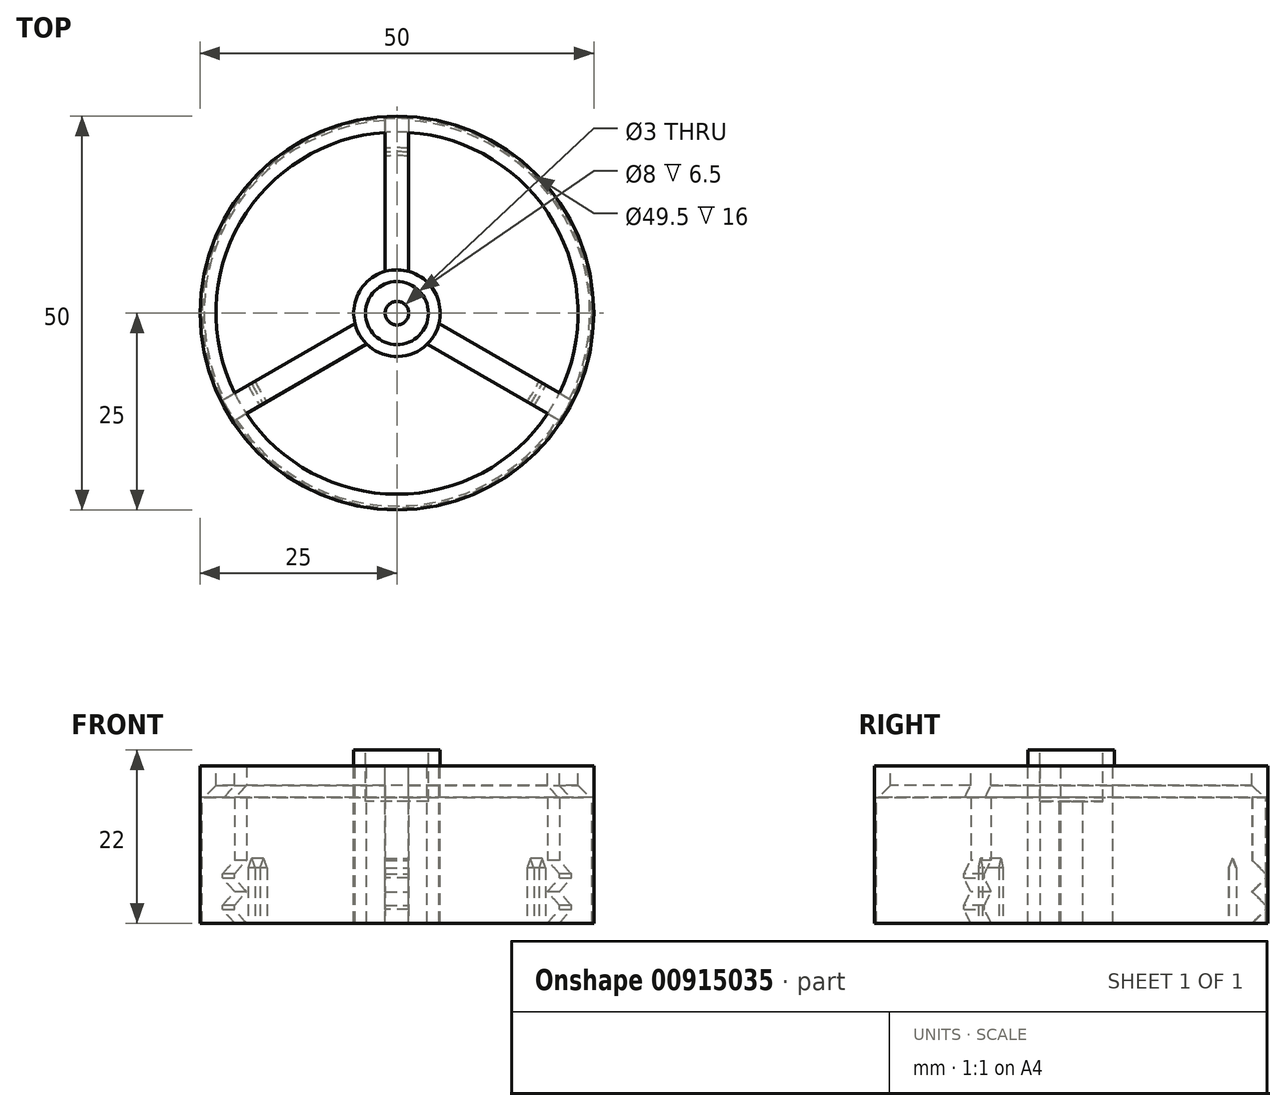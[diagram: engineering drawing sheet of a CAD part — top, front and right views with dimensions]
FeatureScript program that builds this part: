
annotation { "Feature Type Name" : "Feature", "Feature Type Description" : "" }
export const myFeature = defineFeature(function(context is Context, id is Id, definition is map)
    precondition{}
    {
        {
            var Q0;
            Q0=qCreatedBy(makeId("Front.planeOp"),FACE);
            var sketch = newSketch(context, id + "F0", { "sketchPlane" : qUnion([Q0])});
            skLineSegment(sketch, "E0", {"start": v(23, 0) * mm, "end": v(23, 12) * mm});
            skLineSegment(sketch, "E1", {"start": v(23, 12) * mm, "end": v(25, 14) * mm});
            skLineSegment(sketch, "E2", {"start": v(25, 14) * mm, "end": v(23, 16) * mm});
            skLineSegment(sketch, "E3", {"start": v(23, 16) * mm, "end": v(25, 18) * mm});
            skLineSegment(sketch, "E4", {"start": v(25, 18) * mm, "end": v(23, 20) * mm});
            skLineSegment(sketch, "E5", {"start": v(23, 20) * mm, "end": v(0, 20) * mm});
            skLineSegment(sketch, "E6", {"start": v(0, 20) * mm, "end": v(0, 0) * mm});
            skLineSegment(sketch, "E7", {"start": v(0, 0) * mm, "end": v(23, 0) * mm});
            skLineSegment(sketch, "E8", {"start": v(21, 20) * mm, "end": v(21, 13) * mm});
            skLineSegment(sketch, "E9", {"start": v(20, 13) * mm, "end": v(20, 20) * mm});
            skLineSegment(sketch, "E10", {"start": v(20, 13) * mm, "end": v(20.5, 11.8) * mm});
            skLineSegment(sketch, "E11", {"start": v(20.5, 11.8) * mm, "end": v(21, 13) * mm});
            skSolve(sketch);
        }
        {
            var Q0;
            Q0=makeQuery(id+"F0.imprint","IMPRINT",FACE,{"disambiguationData":[TD([[makeQuery(id+"F0.imprint","IMPRINT",EDGE,{"derivedFrom":sQuery(id+"F0.wireOp",EDGE,"E0")}),1.0]])]});
            var Q1;
            Q1=sQuery(id+"F0.wireOp",EDGE,"E6");
            revolve(context, id + "F1", {"surfaceOperationType" : NewSurfaceOperationType.NEW, "entities" : qUnion([Q0]), "axis" : qUnion([Q1]), "revolveType" : RevolveType.FULL});
        }
        {
            var Q0;
            Q0=qCreatedBy(makeId("Top.planeOp"),FACE);
            var sketch = newSketch(context, id + "F2", { "sketchPlane" : qUnion([Q0])});
            skCircle(sketch, "E12", {"center": v(0, 0) * mm, "radius": 25 * mm});
            skCircle(sketch, "E13", {"center": v(0, 0) * mm, "radius": 4 * mm});
            skCircle(sketch, "E14", {"center": v(0, 0) * mm, "radius": 5.5 * mm});
            skLineSegment(sketch, "E15", {"start": v(-31.51, 0) * mm, "end": v(37.3, 0) * mm, "construction": true});
            skLineSegment(sketch, "E16", {"start": v(0, 27.34) * mm, "end": v(0, -29.3) * mm, "construction": true});
            skLineSegment(sketch, "E17", {"start": v(-1.5, -5.3) * mm, "end": v(-1.5, -24.95) * mm});
            skLineSegment(sketch, "E18", {"start": v(1.5, -5.3) * mm, "end": v(1.5, -24.95) * mm});
            skLineSegment(sketch, "E19", {"start": v(-5.33, 1.35) * mm, "end": v(-22.36, 11.18) * mm});
            skLineSegment(sketch, "E20", {"start": v(-3.83, 3.94) * mm, "end": v(-20.86, 13.78) * mm});
            skLineSegment(sketch, "E21", {"start": v(3.83, 3.94) * mm, "end": v(20.86, 13.78) * mm});
            skLineSegment(sketch, "E22", {"start": v(5.33, 1.35) * mm, "end": v(22.36, 11.18) * mm});
            skLineSegment(sketch, "E23", {"start": v(0, 0) * mm, "end": v(34.28, 19.79) * mm, "construction": true});
            skLineSegment(sketch, "E24", {"start": v(0, 0) * mm, "end": v(-31.49, 18.18) * mm, "construction": true});
            skCircle(sketch, "E25", {"center": v(0, 0) * mm, "radius": 1.5 * mm});
            skCircle(sketch, "E26", {"center": v(0, 0) * mm, "radius": 23 * mm});
            skCircle(sketch, "E27", {"center": v(0, 0) * mm, "radius": 24.75 * mm});
            skSolve(sketch);
        }
        {
            var Q0;
            {var subQ0=sQuery(id+"F2.wireOp",EDGE,"E17");Q0=makeQuery(id+"F2.imprint","IMPRINT",FACE,{"disambiguationData":[TD([[makeQuery(id+"F2.imprint","IMPRINT",EDGE,{"derivedFrom":subQ0}),-1.0]])]});}
            var Q1;
            {var subQ0=sQuery(id+"F2.wireOp",EDGE,"E18");Q1=makeQuery(id+"F2.imprint","IMPRINT",FACE,{"disambiguationData":[TD([[makeQuery(id+"F2.imprint","IMPRINT",EDGE,{"derivedFrom":subQ0}),1.0]])]});}
            var Q2;
            {var subQ0=sQuery(id+"F2.wireOp",EDGE,"E20");Q2=makeQuery(id+"F2.imprint","IMPRINT",FACE,{"disambiguationData":[TD([[makeQuery(id+"F2.imprint","IMPRINT",EDGE,{"derivedFrom":subQ0}),-1.0]])]});}
            var Q3;
            Q3=makeQuery(id+"F2.imprint","IMPRINT",FACE,{"disambiguationData":[TD([[makeQuery(id+"F2.imprint","IMPRINT",EDGE,{"derivedFrom":sQuery(id+"F2.wireOp",EDGE,"E25")}),1.0]])]});
            var Q4;
            Q4=makeQuery(id+"F1.opRevolve","SWEPT_FACE",FACE,{"disambiguationData":[OSD([sQuery(id+"F0.wireOp",EDGE,"E5")])]});
            extrude(context, id + "F3", {"entities" : qUnion([Q0, Q1, Q2, Q3]), "operationType" : NewBodyOperationType.REMOVE, "endBound" : BoundingType.UP_TO_SURFACE, "depth" : 25 * mm, "endBoundEntityFace" : qUnion([Q4]), "offsetDistance" : 25 * mm});
        }
        {
            var Q0;
            Q0=makeQuery(id+"F2.imprint","IMPRINT",FACE,{"disambiguationData":[TD([[makeQuery(id+"F2.imprint","IMPRINT",EDGE,{"derivedFrom":sQuery(id+"F2.wireOp",EDGE,"E13")}),1.0]])]});
            extrude(context, id + "F4", {"entities" : qUnion([Q0]), "operationType" : NewBodyOperationType.REMOVE, "depth" : 4.5 * mm, "offsetDistance" : 25 * mm});
        }
        {
            var Q0;
            {var subQ0=sQuery(id+"F2.wireOp",EDGE,"E20");var subQ1=sQuery(id+"F2.wireOp",EDGE,"E12");var subQ2=makeQuery(id+"F2.imprint","INTERSECT",VERTEX,{"derivedFrom":[subQ1,subQ0]});Q0=makeQuery(id+"F2.imprint","IMPRINT",FACE,{"disambiguationData":[TD([[makeQuery(id+"F2.imprint","IMPRINT",EDGE,{"disambiguationData":[TD([[subQ2,1.0]])],"derivedFrom":subQ1}),1.0]])]});}
            var Q1;
            {var subQ0=sQuery(id+"F2.wireOp",EDGE,"E19");var subQ1=sQuery(id+"F2.wireOp",EDGE,"E12");var subQ2=makeQuery(id+"F2.imprint","INTERSECT",VERTEX,{"derivedFrom":[subQ1,subQ0]});Q1=makeQuery(id+"F2.imprint","IMPRINT",FACE,{"disambiguationData":[TD([[makeQuery(id+"F2.imprint","IMPRINT",EDGE,{"disambiguationData":[TD([[subQ2,1.0]])],"derivedFrom":subQ1}),1.0]])]});}
            var Q2;
            {var subQ0=sQuery(id+"F2.wireOp",EDGE,"E17");var subQ1=sQuery(id+"F2.wireOp",EDGE,"E12");var subQ2=makeQuery(id+"F2.imprint","INTERSECT",VERTEX,{"derivedFrom":[subQ1,subQ0]});Q2=makeQuery(id+"F2.imprint","IMPRINT",FACE,{"disambiguationData":[TD([[makeQuery(id+"F2.imprint","IMPRINT",EDGE,{"disambiguationData":[TD([[subQ2,1.0]])],"derivedFrom":subQ1}),1.0]])]});}
            var Q3;
            {var subQ0=sQuery(id+"F2.wireOp",EDGE,"E17");var subQ1=sQuery(id+"F2.wireOp",EDGE,"E12");var subQ2=makeQuery(id+"F2.imprint","INTERSECT",VERTEX,{"derivedFrom":[subQ1,subQ0]});Q3=makeQuery(id+"F2.imprint","IMPRINT",FACE,{"disambiguationData":[TD([[makeQuery(id+"F2.imprint","IMPRINT",EDGE,{"disambiguationData":[TD([[subQ2,-1.0]])],"derivedFrom":subQ1}),1.0]])]});}
            var Q4;
            {var subQ0=sQuery(id+"F2.wireOp",EDGE,"E18");var subQ1=sQuery(id+"F2.wireOp",EDGE,"E12");var subQ2=makeQuery(id+"F2.imprint","INTERSECT",VERTEX,{"derivedFrom":[subQ1,subQ0]});Q4=makeQuery(id+"F2.imprint","IMPRINT",FACE,{"disambiguationData":[TD([[makeQuery(id+"F2.imprint","IMPRINT",EDGE,{"disambiguationData":[TD([[subQ2,-1.0]])],"derivedFrom":subQ1}),1.0]])]});}
            var Q5;
            {var subQ0=sQuery(id+"F2.wireOp",EDGE,"E21");var subQ1=sQuery(id+"F2.wireOp",EDGE,"E12");var subQ2=makeQuery(id+"F2.imprint","INTERSECT",VERTEX,{"derivedFrom":[subQ1,subQ0]});Q5=makeQuery(id+"F2.imprint","IMPRINT",FACE,{"disambiguationData":[TD([[makeQuery(id+"F2.imprint","IMPRINT",EDGE,{"disambiguationData":[TD([[subQ2,1.0]])],"derivedFrom":subQ1}),1.0]])]});}
            var Q6;
            {var subQ0=sQuery(id+"F2.wireOp",EDGE,"E18");var subQ1=sQuery(id+"F2.wireOp",EDGE,"E12");var subQ2=makeQuery(id+"F2.imprint","INTERSECT",VERTEX,{"derivedFrom":[subQ1,subQ0]});Q6=makeQuery(id+"F2.imprint","IMPRINT",FACE,{"disambiguationData":[TD([[makeQuery(id+"F2.imprint","IMPRINT",EDGE,{"disambiguationData":[TD([[subQ2,-1.0]])],"derivedFrom":subQ1}),1.0]])]});}
            var Q7;
            {var subQ0=sQuery(id+"F2.wireOp",EDGE,"E26");var subQ1=sQuery(id+"F2.wireOp",EDGE,"E18");var subQ2=makeQuery(id+"F2.imprint","INTERSECT",VERTEX,{"derivedFrom":[subQ1,subQ0]});Q7=makeQuery(id+"F2.imprint","IMPRINT",FACE,{"disambiguationData":[TD([[makeQuery(id+"F2.imprint","IMPRINT",EDGE,{"disambiguationData":[TD([[subQ2,-1.0]])],"derivedFrom":subQ1}),1.0]])]});}
            var Q8;
            {var subQ0=sQuery(id+"F2.wireOp",EDGE,"E26");var subQ1=sQuery(id+"F2.wireOp",EDGE,"E21");var subQ2=makeQuery(id+"F2.imprint","INTERSECT",VERTEX,{"derivedFrom":[subQ1,subQ0]});Q8=makeQuery(id+"F2.imprint","IMPRINT",FACE,{"disambiguationData":[TD([[makeQuery(id+"F2.imprint","IMPRINT",EDGE,{"disambiguationData":[TD([[subQ2,-1.0]])],"derivedFrom":subQ1}),-1.0]])]});}
            var Q9;
            {var subQ0=sQuery(id+"F2.wireOp",EDGE,"E21");var subQ1=sQuery(id+"F2.wireOp",EDGE,"E12");var subQ2=makeQuery(id+"F2.imprint","INTERSECT",VERTEX,{"derivedFrom":[subQ1,subQ0]});Q9=makeQuery(id+"F2.imprint","IMPRINT",FACE,{"disambiguationData":[TD([[makeQuery(id+"F2.imprint","IMPRINT",EDGE,{"disambiguationData":[TD([[subQ2,1.0]])],"derivedFrom":subQ1}),1.0]])]});}
            var Q10;
            {var subQ0=sQuery(id+"F2.wireOp",EDGE,"E20");var subQ1=sQuery(id+"F2.wireOp",EDGE,"E12");var subQ2=makeQuery(id+"F2.imprint","INTERSECT",VERTEX,{"derivedFrom":[subQ1,subQ0]});Q10=makeQuery(id+"F2.imprint","IMPRINT",FACE,{"disambiguationData":[TD([[makeQuery(id+"F2.imprint","IMPRINT",EDGE,{"disambiguationData":[TD([[subQ2,1.0]])],"derivedFrom":subQ1}),1.0]])]});}
            var Q11;
            {var subQ0=sQuery(id+"F2.wireOp",EDGE,"E26");var subQ1=sQuery(id+"F2.wireOp",EDGE,"E20");var subQ2=makeQuery(id+"F2.imprint","INTERSECT",VERTEX,{"derivedFrom":[subQ1,subQ0]});Q11=makeQuery(id+"F2.imprint","IMPRINT",FACE,{"disambiguationData":[TD([[makeQuery(id+"F2.imprint","IMPRINT",EDGE,{"disambiguationData":[TD([[subQ2,-1.0]])],"derivedFrom":subQ1}),-1.0]])]});}
            var Q12;
            {var subQ0=sQuery(id+"F2.wireOp",EDGE,"E26");var subQ1=sQuery(id+"F2.wireOp",EDGE,"E17");var subQ2=makeQuery(id+"F2.imprint","INTERSECT",VERTEX,{"derivedFrom":[subQ1,subQ0]});Q12=makeQuery(id+"F2.imprint","IMPRINT",FACE,{"disambiguationData":[TD([[makeQuery(id+"F2.imprint","IMPRINT",EDGE,{"disambiguationData":[TD([[subQ2,-1.0]])],"derivedFrom":subQ1}),1.0]])]});}
            var Q13;
            {var subQ0=sQuery(id+"F2.wireOp",EDGE,"E17");var subQ1=sQuery(id+"F2.wireOp",EDGE,"E12");var subQ2=makeQuery(id+"F2.imprint","INTERSECT",VERTEX,{"derivedFrom":[subQ1,subQ0]});Q13=makeQuery(id+"F2.imprint","IMPRINT",FACE,{"disambiguationData":[TD([[makeQuery(id+"F2.imprint","IMPRINT",EDGE,{"disambiguationData":[TD([[subQ2,-1.0]])],"derivedFrom":subQ1}),1.0]])]});}
            var Q14;
            {var subQ0=sQuery(id+"F2.wireOp",EDGE,"E26");var subQ1=sQuery(id+"F2.wireOp",EDGE,"E17");var subQ2=makeQuery(id+"F2.imprint","INTERSECT",VERTEX,{"derivedFrom":[subQ1,subQ0]});Q14=makeQuery(id+"F2.imprint","IMPRINT",FACE,{"disambiguationData":[TD([[makeQuery(id+"F2.imprint","IMPRINT",EDGE,{"disambiguationData":[TD([[subQ2,-1.0]])],"derivedFrom":subQ1}),-1.0]])]});}
            var Q15;
            {var subQ0=sQuery(id+"F2.wireOp",EDGE,"E17");var subQ1=sQuery(id+"F2.wireOp",EDGE,"E12");var subQ2=makeQuery(id+"F2.imprint","INTERSECT",VERTEX,{"derivedFrom":[subQ1,subQ0]});Q15=makeQuery(id+"F2.imprint","IMPRINT",FACE,{"disambiguationData":[TD([[makeQuery(id+"F2.imprint","IMPRINT",EDGE,{"disambiguationData":[TD([[subQ2,1.0]])],"derivedFrom":subQ1}),1.0]])]});}
            var Q16;
            {var subQ0=sQuery(id+"F2.wireOp",EDGE,"E26");var subQ1=sQuery(id+"F2.wireOp",EDGE,"E19");var subQ2=makeQuery(id+"F2.imprint","INTERSECT",VERTEX,{"derivedFrom":[subQ1,subQ0]});Q16=makeQuery(id+"F2.imprint","IMPRINT",FACE,{"disambiguationData":[TD([[makeQuery(id+"F2.imprint","IMPRINT",EDGE,{"disambiguationData":[TD([[subQ2,-1.0]])],"derivedFrom":subQ1}),-1.0]])]});}
            var Q17;
            {var subQ0=sQuery(id+"F2.wireOp",EDGE,"E19");var subQ1=sQuery(id+"F2.wireOp",EDGE,"E12");var subQ2=makeQuery(id+"F2.imprint","INTERSECT",VERTEX,{"derivedFrom":[subQ1,subQ0]});Q17=makeQuery(id+"F2.imprint","IMPRINT",FACE,{"disambiguationData":[TD([[makeQuery(id+"F2.imprint","IMPRINT",EDGE,{"disambiguationData":[TD([[subQ2,1.0]])],"derivedFrom":subQ1}),1.0]])]});}
            extrude(context, id + "F5", {"entities" : qUnion([Q0, Q1, Q2, Q3, Q4, Q5, Q6, Q7, Q8, Q9, Q10, Q11, Q12, Q13, Q14, Q15, Q16, Q17]), "operationType" : NewBodyOperationType.ADD, "depth" : 4 * mm, "offsetDistance" : 25 * mm});
        }
        {
            var Q0;
            {var subQ0=sQuery(id+"F2.wireOp",EDGE,"E20");var subQ1=sQuery(id+"F2.wireOp",EDGE,"E12");var subQ2=makeQuery(id+"F2.imprint","INTERSECT",VERTEX,{"derivedFrom":[subQ1,subQ0]});Q0=makeQuery(id+"F2.imprint","IMPRINT",FACE,{"disambiguationData":[TD([[makeQuery(id+"F2.imprint","IMPRINT",EDGE,{"disambiguationData":[TD([[subQ2,1.0]])],"derivedFrom":subQ1}),1.0]])]});}
            var Q1;
            {var subQ0=sQuery(id+"F2.wireOp",EDGE,"E21");var subQ1=sQuery(id+"F2.wireOp",EDGE,"E12");var subQ2=makeQuery(id+"F2.imprint","INTERSECT",VERTEX,{"derivedFrom":[subQ1,subQ0]});Q1=makeQuery(id+"F2.imprint","IMPRINT",FACE,{"disambiguationData":[TD([[makeQuery(id+"F2.imprint","IMPRINT",EDGE,{"disambiguationData":[TD([[subQ2,1.0]])],"derivedFrom":subQ1}),1.0]])]});}
            var Q2;
            {var subQ0=sQuery(id+"F2.wireOp",EDGE,"E18");var subQ1=sQuery(id+"F2.wireOp",EDGE,"E12");var subQ2=makeQuery(id+"F2.imprint","INTERSECT",VERTEX,{"derivedFrom":[subQ1,subQ0]});Q2=makeQuery(id+"F2.imprint","IMPRINT",FACE,{"disambiguationData":[TD([[makeQuery(id+"F2.imprint","IMPRINT",EDGE,{"disambiguationData":[TD([[subQ2,-1.0]])],"derivedFrom":subQ1}),1.0]])]});}
            var Q3;
            {var subQ0=sQuery(id+"F2.wireOp",EDGE,"E17");var subQ1=sQuery(id+"F2.wireOp",EDGE,"E12");var subQ2=makeQuery(id+"F2.imprint","INTERSECT",VERTEX,{"derivedFrom":[subQ1,subQ0]});Q3=makeQuery(id+"F2.imprint","IMPRINT",FACE,{"disambiguationData":[TD([[makeQuery(id+"F2.imprint","IMPRINT",EDGE,{"disambiguationData":[TD([[subQ2,-1.0]])],"derivedFrom":subQ1}),1.0]])]});}
            var Q4;
            {var subQ0=sQuery(id+"F2.wireOp",EDGE,"E17");var subQ1=sQuery(id+"F2.wireOp",EDGE,"E12");var subQ2=makeQuery(id+"F2.imprint","INTERSECT",VERTEX,{"derivedFrom":[subQ1,subQ0]});Q4=makeQuery(id+"F2.imprint","IMPRINT",FACE,{"disambiguationData":[TD([[makeQuery(id+"F2.imprint","IMPRINT",EDGE,{"disambiguationData":[TD([[subQ2,1.0]])],"derivedFrom":subQ1}),1.0]])]});}
            var Q5;
            {var subQ0=sQuery(id+"F2.wireOp",EDGE,"E19");var subQ1=sQuery(id+"F2.wireOp",EDGE,"E12");var subQ2=makeQuery(id+"F2.imprint","INTERSECT",VERTEX,{"derivedFrom":[subQ1,subQ0]});Q5=makeQuery(id+"F2.imprint","IMPRINT",FACE,{"disambiguationData":[TD([[makeQuery(id+"F2.imprint","IMPRINT",EDGE,{"disambiguationData":[TD([[subQ2,1.0]])],"derivedFrom":subQ1}),1.0]])]});}
            extrude(context, id + "F6", {"entities" : qUnion([Q0, Q1, Q2, Q3, Q4, Q5]), "operationType" : NewBodyOperationType.ADD, "depth" : 20 * mm, "offsetDistance" : 25 * mm});
        }
        {
            var Q0;
            {var subQ0=sQuery(id+"F2.wireOp",EDGE,"E26");var subQ1=makeQuery(id+"F5.opExtrude","CAP_FACE",FACE,{"disambiguationData":[OSD([sQuery(id+"F2.wireOp",EDGE,"E12"),subQ0])],"isStart":false});var subQ2=makeQuery(id+"F5.opExtrude","SWEPT_FACE",FACE,{"disambiguationData":[OSD([subQ0])]});Q0=makeQuery(id+"F5.boolean.opBoolean","SPLIT",EDGE,{"disambiguationData":[topologyDisambiguationEdgeConnected([subQ1,subQ2]),TD([makeQuery(id+"F3.boolean.opBoolean","COPY",FACE,{"derivedFrom":makeQuery(id+"F3.opExtrude","SWEPT_FACE",FACE,{"disambiguationData":[OSD([sQuery(id+"F2.wireOp",EDGE,"E17")])]})})])],"derivedFrom":makeQuery(id+"F5.opExtrude","CAP_EDGE",EDGE,{"disambiguationData":[OSD([subQ0])],"isStart":false})});}
            var Q1;
            {var subQ0=sQuery(id+"F2.wireOp",EDGE,"E26");var subQ1=makeQuery(id+"F5.opExtrude","CAP_FACE",FACE,{"disambiguationData":[OSD([sQuery(id+"F2.wireOp",EDGE,"E12"),subQ0])],"isStart":false});var subQ2=makeQuery(id+"F5.opExtrude","SWEPT_FACE",FACE,{"disambiguationData":[OSD([subQ0])]});Q1=makeQuery(id+"F5.boolean.opBoolean","SPLIT",EDGE,{"disambiguationData":[topologyDisambiguationEdgeConnected([subQ1,subQ2]),TD([makeQuery(id+"F3.boolean.opBoolean","COPY",FACE,{"derivedFrom":makeQuery(id+"F3.opExtrude","SWEPT_FACE",FACE,{"disambiguationData":[OSD([sQuery(id+"F2.wireOp",EDGE,"E18")])]})})])],"derivedFrom":makeQuery(id+"F5.opExtrude","CAP_EDGE",EDGE,{"disambiguationData":[OSD([subQ0])],"isStart":false})});}
            var Q2;
            {var subQ0=sQuery(id+"F2.wireOp",EDGE,"E26");var subQ1=makeQuery(id+"F5.opExtrude","CAP_FACE",FACE,{"disambiguationData":[OSD([sQuery(id+"F2.wireOp",EDGE,"E12"),subQ0])],"isStart":false});var subQ2=makeQuery(id+"F5.opExtrude","SWEPT_FACE",FACE,{"disambiguationData":[OSD([subQ0])]});Q2=makeQuery(id+"F5.boolean.opBoolean","SPLIT",EDGE,{"disambiguationData":[topologyDisambiguationEdgeConnected([subQ1,subQ2]),TD([makeQuery(id+"F3.boolean.opBoolean","COPY",FACE,{"derivedFrom":makeQuery(id+"F3.opExtrude","SWEPT_FACE",FACE,{"disambiguationData":[OSD([sQuery(id+"F2.wireOp",EDGE,"E20")])]})})])],"derivedFrom":makeQuery(id+"F5.opExtrude","CAP_EDGE",EDGE,{"disambiguationData":[OSD([subQ0])],"isStart":false})});}
            chamfer(context, id + "F7", {"entities" : qUnion([Q0, Q1, Q2]), "width" : 1.5 * mm, "tangentPropagation" : true});
        }
        {
            var Q0;
            Q0=makeQuery(id+"F2.imprint","IMPRINT",FACE,{"disambiguationData":[TD([[makeQuery(id+"F2.imprint","IMPRINT",EDGE,{"derivedFrom":sQuery(id+"F2.wireOp",EDGE,"E13")}),-1.0]])]});
            extrude(context, id + "F8", {"entities" : qUnion([Q0]), "operationType" : NewBodyOperationType.ADD, "oppositeDirection" : true, "depth" : 2 * mm, "offsetDistance" : 25 * mm});
        }
        {
            var Q0;
            Q0=makeQuery(id+"F1.opRevolve","SWEPT_BODY",BODY,{"disambiguationData":[OSD([sQuery(id+"F0.wireOp",EDGE,"E0"),sQuery(id+"F0.wireOp",EDGE,"E1"),sQuery(id+"F0.wireOp",EDGE,"E2"),sQuery(id+"F0.wireOp",EDGE,"E3"),sQuery(id+"F0.wireOp",EDGE,"E4"),sQuery(id+"F0.wireOp",EDGE,"E5"),sQuery(id+"F0.wireOp",EDGE,"E6"),sQuery(id+"F0.wireOp",EDGE,"E7")])]});
            var Q1;
            Q1=sQuery(id+"F2.wireOp",EDGE,"E15");
            transform(context, id + "F9", {"entities" : qUnion([Q0]), "transformType" : TransformType.ROTATION, "transformAxis" : qUnion([Q1]), "angle" : 180 * degree, "makeCopy" : false});
        }
    });
